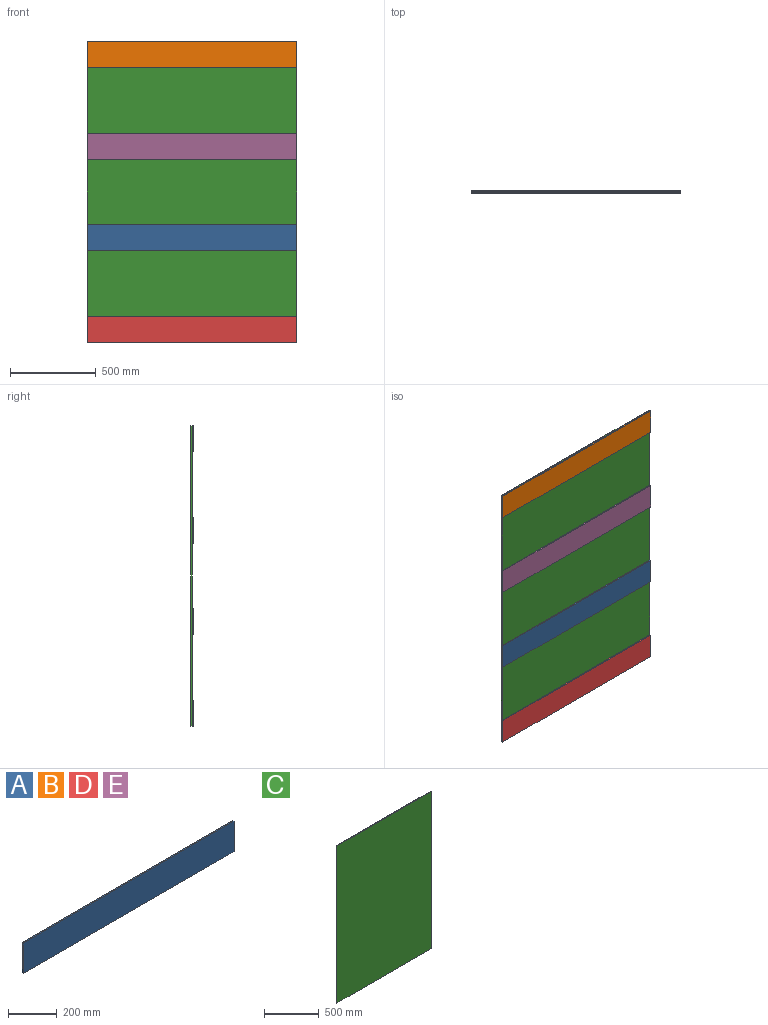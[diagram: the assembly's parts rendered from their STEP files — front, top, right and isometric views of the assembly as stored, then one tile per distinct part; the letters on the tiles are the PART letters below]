
ASSEMBLY  parts=5 mates=4
PART A: 6 faces, bbox 1219.2x6.4x152.4 mm
  f0: plane 152.4x6.35mm, normal (-1,0,0), area 967.7mm2, adj f1,f3,f4,f5
  f1: plane 1219.2x6.35mm, normal (0,0,-1), area 7741.9mm2, adj f0,f2,f4,f5
  f2: plane 152.4x6.35mm, normal (1,0,0), area 967.7mm2, adj f1,f3,f4,f5
  f3: plane 1219.2x6.35mm, normal (0,0,1), area 7741.9mm2, adj f0,f2,f4,f5
  f4: plane 1219.2x152.4mm, normal (0,-1,0), area 185806.1mm2, adj f0,f1,f2,f3
  f5: plane 1219.2x152.4mm, normal (0,1,0), area 185806.1mm2, adj f0,f1,f2,f3
PART B: same geometry as A
PART C: 6 faces, bbox 1219.2x6.4x1752.6 mm
  f0: plane 1752.6x6.35mm, normal (-1,0,0), area 11129mm2, adj f1,f3,f4,f5
  f1: plane 1219.2x6.35mm, normal (0,0,-1), area 7741.9mm2, adj f0,f2,f4,f5
  f2: plane 1752.6x6.35mm, normal (1,0,0), area 11129mm2, adj f1,f3,f4,f5
  f3: plane 1219.2x6.35mm, normal (0,0,1), area 7741.9mm2, adj f0,f2,f4,f5
  f4: plane 1752.6x1219.2mm, normal (0,-1,0), area 2136769.9mm2, adj f0,f1,f2,f3
  f5: plane 1752.6x1219.2mm, normal (0,1,0), area 2136769.9mm2, adj f0,f1,f2,f3
PART D: same geometry as A
PART E: same geometry as A
PLACE A t=(-267.41,19.05,521.2)mm
PLACE B t=(-267.41,19.05,1588)mm
PLACE C t=(-267.41,25.4,-12.2)mm
PLACE D t=(-267.41,19.05,-12.2)mm
PLACE E t=(-267.41,19.05,1054.6)mm
MATE fastened D.f5 <-> C.f4  axis (0,1,0) through (342.19,19.05,64)mm
MATE fastened E.f5 <-> C.f4  axis (0,1,0) through (342.19,19.05,1130.8)mm
MATE fastened A.f5 <-> C.f4  axis (0,1,0) through (342.19,19.05,597.4)mm
MATE fastened B.f5 <-> C.f4  axis (0,1,0) through (342.19,19.05,1664.2)mm
